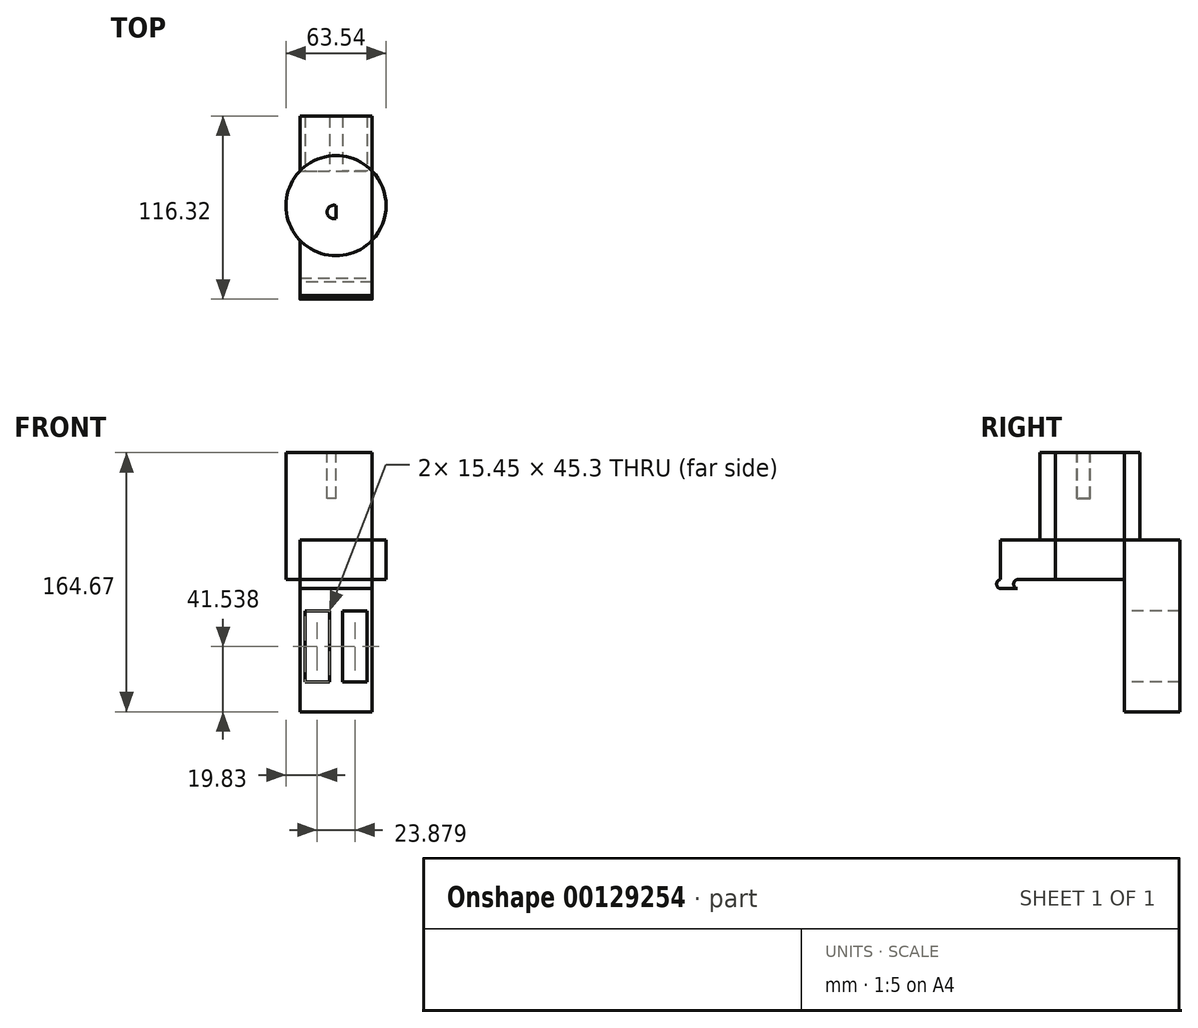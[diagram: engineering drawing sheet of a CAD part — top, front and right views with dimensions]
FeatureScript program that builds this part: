
annotation { "Feature Type Name" : "Feature", "Feature Type Description" : "" }
export const myFeature = defineFeature(function(context is Context, id is Id, definition is map)
    precondition{}
    {
        {
            var Q0;
            Q0=qCreatedBy(makeId("Top.planeOp"),FACE);
            var sketch = newSketch(context, id + "F0", { "sketchPlane" : qUnion([Q0])});
            skCircle(sketch, "E0", {"center": v(0, 0) * mm, "radius": 31.77 * mm});
            skLineSegment(sketch, "E1.bottom", {"start": v(22.97, -56.95) * mm, "end": v(-22.97, -56.95) * mm});
            skLineSegment(sketch, "E1.top", {"start": v(22.97, 56.95) * mm, "end": v(-22.97, 56.95) * mm});
            skLineSegment(sketch, "E1.left", {"start": v(22.97, -56.95) * mm, "end": v(22.97, 56.95) * mm});
            skLineSegment(sketch, "E1.right", {"start": v(-22.97, -56.95) * mm, "end": v(-22.97, 56.95) * mm});
            skSolve(sketch);
        }
        {
            var Q0;
            {var subQ0=sQuery(id+"F0.wireOp",EDGE,"E1.left");var subQ1=sQuery(id+"F0.wireOp",EDGE,"E0");var subQ2=makeQuery(id+"F0.imprint","INTERSECT",VERTEX,{"disambiguationData":[OD(0.0)],"derivedFrom":[subQ1,subQ0]});Q0=makeQuery(id+"F0.imprint","IMPRINT",FACE,{"disambiguationData":[TD([[makeQuery(id+"F0.imprint","IMPRINT",EDGE,{"disambiguationData":[TD([[subQ2,1.0]])],"derivedFrom":subQ1}),1.0]])]});}
            var Q1;
            {var subQ0=sQuery(id+"F0.wireOp",EDGE,"E1.right");var subQ1=sQuery(id+"F0.wireOp",EDGE,"E0");var subQ2=makeQuery(id+"F0.imprint","INTERSECT",VERTEX,{"disambiguationData":[OD(0.0)],"derivedFrom":[subQ1,subQ0]});Q1=makeQuery(id+"F0.imprint","IMPRINT",FACE,{"disambiguationData":[TD([[makeQuery(id+"F0.imprint","IMPRINT",EDGE,{"disambiguationData":[TD([[subQ2,1.0]])],"derivedFrom":subQ1}),1.0]])]});}
            var Q2;
            {var subQ0=sQuery(id+"F0.wireOp",EDGE,"E1.right");var subQ1=sQuery(id+"F0.wireOp",EDGE,"E0");var subQ2=makeQuery(id+"F0.imprint","INTERSECT",VERTEX,{"disambiguationData":[OD(0.0)],"derivedFrom":[subQ1,subQ0]});Q2=makeQuery(id+"F0.imprint","IMPRINT",FACE,{"disambiguationData":[TD([[makeQuery(id+"F0.imprint","IMPRINT",EDGE,{"disambiguationData":[TD([[subQ2,-1.0]])],"derivedFrom":subQ1}),1.0]])]});}
            extrude(context, id + "F1", {"entities" : qUnion([Q0, Q1, Q2]), "depth" : 80.54 * mm});
        }
        {
            var Q0;
            Q0 = qSketchRegion(id + "F0", true);
            extrude(context, id + "F2", {"entities" : qUnion([Q0]), "operationType" : NewBodyOperationType.ADD, "depth" : 25 * mm});
        }
        {
            var Q0;
            {var subQ0=sQuery(id+"F0.wireOp",EDGE,"E0");Q0=makeQuery(id+"F2.boolean.opBoolean","MERGE",FACE,{"derivedFrom":[makeQuery(id+"F1.opExtrude","CAP_FACE",FACE,{"disambiguationData":[OSD([subQ0])],"isStart":true}),makeQuery(id+"F2.opExtrude","CAP_FACE",FACE,{"disambiguationData":[OSD([subQ0,sQuery(id+"F0.wireOp",EDGE,"E1.bottom"),sQuery(id+"F0.wireOp",EDGE,"E1.top"),sQuery(id+"F0.wireOp",EDGE,"E1.left"),sQuery(id+"F0.wireOp",EDGE,"E1.right")])],"isStart":true})]});}
            var sketch = newSketch(context, id + "F3", { "sketchPlane" : qUnion([Q0])});
            skLineSegment(sketch, "E2", {"start": v(-22.97, -21.95) * mm, "end": v(22.97, -21.95) * mm});
            skSolve(sketch);
        }
        {
            var Q0;
            Q0=makeQuery(id+"F3.imprint","IMPRINT",FACE,{"disambiguationData":[TD([[makeQuery(id+"F3.imprint","IMPRINT",EDGE,{"derivedFrom":sQuery(id+"F3.wireOp",EDGE,"E2")}),-1.0]])]});
            extrude(context, id + "F4", {"entities" : qUnion([Q0]), "operationType" : NewBodyOperationType.ADD, "depth" : 84.13 * mm});
        }
        {
            var Q0;
            Q0=makeQuery(id+"F4.opExtrude","SWEPT_FACE",FACE,{"disambiguationData":[OSD([sQuery(id+"F3.wireOp",EDGE,"E2")])]});
            var sketch = newSketch(context, id + "F5", { "sketchPlane" : qUnion([Q0])});
            skLineSegment(sketch, "E3", {"start": v(0, 0) * mm, "end": v(0, -84.13) * mm, "construction": true});
            skLineSegment(sketch, "E4.bottom", {"start": v(19.67, -65.24) * mm, "end": v(4.21, -65.24) * mm});
            skLineSegment(sketch, "E4.top", {"start": v(19.67, -19.94) * mm, "end": v(4.21, -19.94) * mm});
            skLineSegment(sketch, "E4.left", {"start": v(19.67, -65.24) * mm, "end": v(19.67, -19.94) * mm});
            skLineSegment(sketch, "E4.right", {"start": v(4.21, -65.24) * mm, "end": v(4.21, -19.94) * mm});
            skLineSegment(sketch, "E5.MirrorCS", {"start": v(-19.67, -19.94) * mm, "end": v(-4.21, -19.94) * mm});
            skLineSegment(sketch, "E6.MirrorCS", {"start": v(-19.67, -65.24) * mm, "end": v(-19.67, -19.94) * mm});
            skLineSegment(sketch, "E7.MirrorCS", {"start": v(-4.21, -65.24) * mm, "end": v(-4.21, -19.94) * mm});
            skLineSegment(sketch, "E8.MirrorCS", {"start": v(-19.67, -65.24) * mm, "end": v(-4.21, -65.24) * mm});
            skSolve(sketch);
        }
        {
            var Q0;
            Q0=makeQuery(id+"F5.imprint","IMPRINT",FACE,{"disambiguationData":[TD([[makeQuery(id+"F5.imprint","IMPRINT",EDGE,{"derivedFrom":sQuery(id+"F5.wireOp",EDGE,"E4.bottom")}),-1.0]])]});
            var Q1;
            Q1=makeQuery(id+"F5.imprint","IMPRINT",FACE,{"disambiguationData":[TD([[makeQuery(id+"F5.imprint","IMPRINT",EDGE,{"derivedFrom":sQuery(id+"F5.wireOp",EDGE,"E5.MirrorCS")}),-1.0]])]});
            extrude(context, id + "F6", {"entities" : qUnion([Q0, Q1]), "operationType" : NewBodyOperationType.REMOVE, "endBound" : BoundingType.THROUGH_ALL, "oppositeDirection" : true, "depth" : 25 * mm});
        }
        {
            var Q0;
            Q0=makeQuery(id+"F1.opExtrude","CAP_FACE",FACE,{"disambiguationData":[OSD([sQuery(id+"F0.wireOp",EDGE,"E0")])],"isStart":false});
            var sketch = newSketch(context, id + "F7", { "sketchPlane" : qUnion([Q0])});
            skArc(sketch, "E9", {"start": v(0, 0) * mm, "mid": v(-5.73, -4.04) * mm, "end": v(0, -8.08) * mm});
            skLineSegment(sketch, "E10", {"start": v(0, -8.08) * mm, "end": v(0, 0) * mm});
            skSolve(sketch);
        }
        {
            var Q0;
            Q0 = qSketchRegion(id + "F7", true);
            extrude(context, id + "F8", {"entities" : qUnion([Q0]), "operationType" : NewBodyOperationType.REMOVE, "oppositeDirection" : true, "depth" : 29.17 * mm});
        }
        {
            var Q0;
            {var subQ0=sQuery(id+"F0.wireOp",EDGE,"E0");Q0=makeQuery(id+"F2.boolean.opBoolean","MERGE",FACE,{"derivedFrom":[makeQuery(id+"F1.opExtrude","CAP_FACE",FACE,{"disambiguationData":[OSD([subQ0])],"isStart":true}),makeQuery(id+"F2.opExtrude","CAP_FACE",FACE,{"disambiguationData":[OSD([subQ0,sQuery(id+"F0.wireOp",EDGE,"E1.bottom"),sQuery(id+"F0.wireOp",EDGE,"E1.top"),sQuery(id+"F0.wireOp",EDGE,"E1.left"),sQuery(id+"F0.wireOp",EDGE,"E1.right")])],"isStart":true})]});}
            var sketch = newSketch(context, id + "F9", { "sketchPlane" : qUnion([Q0])});
            skLineSegment(sketch, "E11", {"start": v(-22.97, 46.13) * mm, "end": v(22.97, 46.13) * mm});
            skSolve(sketch);
        }
        {
            var Q0;
            Q0=qCreatedBy(makeId("Right.planeOp"),FACE);
            var sketch = newSketch(context, id + "F10", { "sketchPlane" : qUnion([Q0])});
            skLineSegment(sketch, "E12.0.0", {"start": v(-56.95, 0) * mm, "end": v(-46.13, 0) * mm});
            skLineSegment(sketch, "E12.0.2", {"start": v(-46.13, 0) * mm, "end": v(-56.95, 0) * mm});
            skArc(sketch, "E13", {"start": v(-51.54, 0) * mm, "mid": v(-53.97, -2.94) * mm, "end": v(-51.54, -5.89) * mm});
            skPoint(sketch, "E13.endSnap0", {"position": v(-51.54, 0) * mm});
            skSolve(sketch);
        }
        {
            var Q0;
            {var subQ0=sQuery(id+"F9.wireOp",EDGE,"E11");Q0=makeQuery(id+"F9.imprint","IMPRINT",FACE,{"disambiguationData":[TD([[makeQuery(id+"F9.imprint","IMPRINT",EDGE,{"derivedFrom":subQ0}),1.0]])]});}
            var Q1;
            Q1=sQuery(id+"F10.wireOp",EDGE,"E13");
            sweep(context, id + "F11", {"operationType" : NewBodyOperationType.ADD, "profiles" : qUnion([Q0]), "path" : qUnion([Q1]), "keepProfileOrientation" : true});
        }
    });
